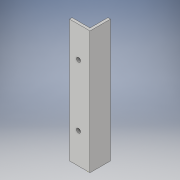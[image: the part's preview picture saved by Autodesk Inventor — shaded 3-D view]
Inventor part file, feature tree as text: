
AUTODESK INVENTOR PART (.ipt)
format: ipt  version: 2018 (Build 220112000, 112)  size: 111,616 bytes
history: native  units: in
note: dims shown in document units (in); Inventor stores cm internally (conversion verified against a paired STEP export)
features: sketch x3, extrude x2
ambient origin geometry x8: Origin, YZ Plane, XZ Plane, XY Plane, X Axis, Y Axis, Z Axis, Center Point
bodies: Solid1 (feature_tree)
feature tree (5):
  extrude  "Extrusion1"  Depth=0.125in
  sketch  "Sketch2"  dims[d2=1.0in d3=0.125in]
  extrude  "Extrusion2"  Depth=0.125in
  sketch  "Sketch1"  dims[d0=1.0in d1=0.125in]
  sketch  "Sketch3"  dims[d4=6.0in d5=0.0in d6=1.5in d7=3.0in d8=0.2in d9=1.0in d10=0.0in]
